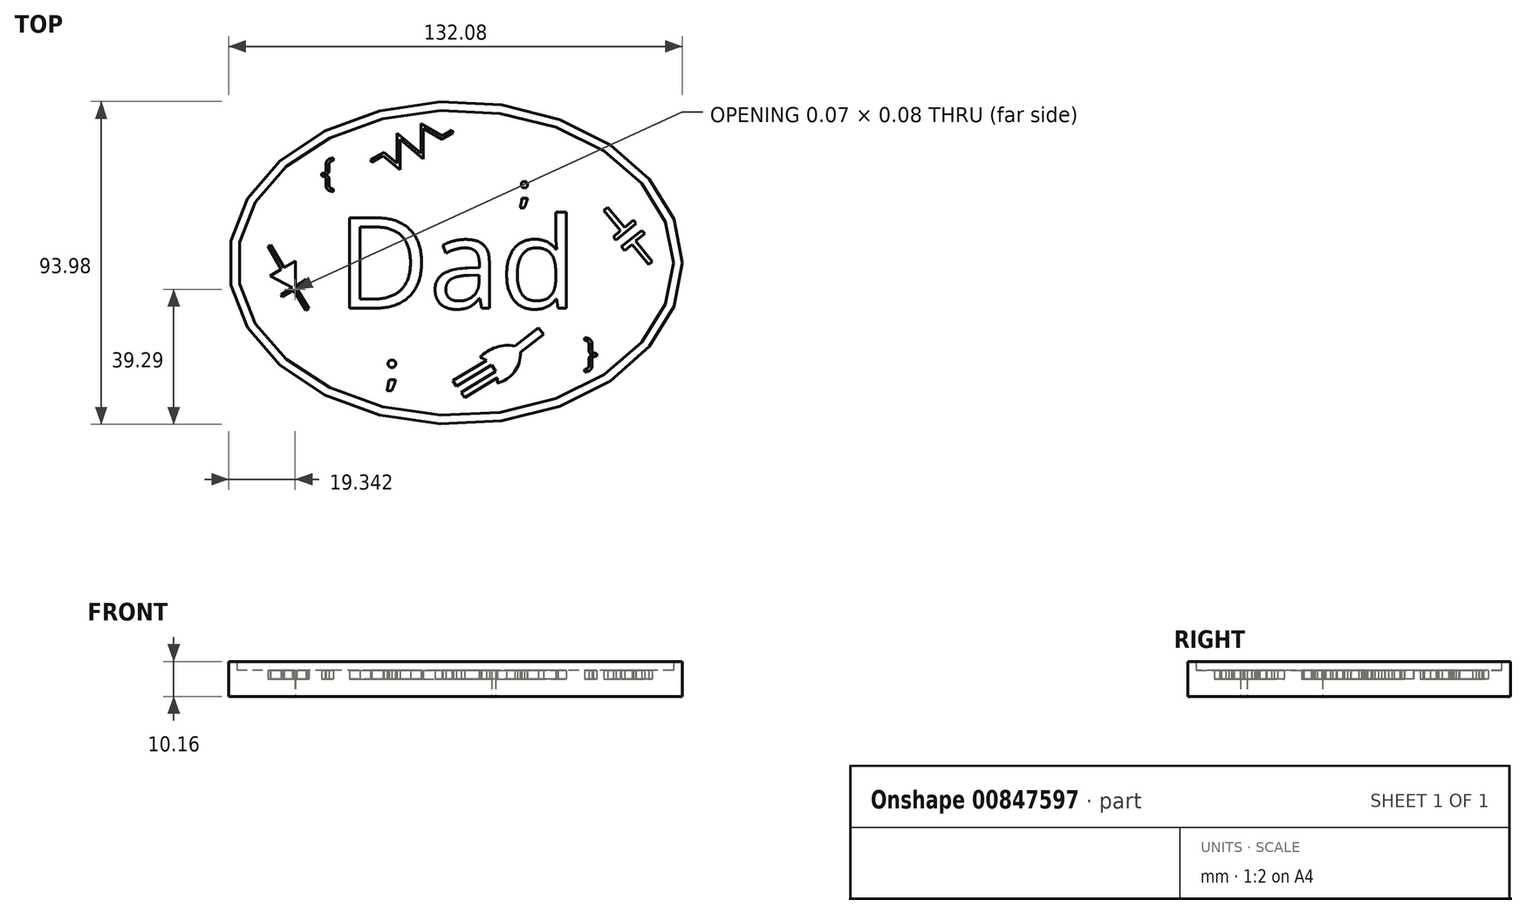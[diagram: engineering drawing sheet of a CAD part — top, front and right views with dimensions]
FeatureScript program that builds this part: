
annotation { "Feature Type Name" : "Feature", "Feature Type Description" : "" }
export const myFeature = defineFeature(function(context is Context, id is Id, definition is map)
    precondition{}
    {
        {
            var Q0;
            Q0=qCreatedBy(makeId("Top.planeOp"),FACE);
            var sketch = newSketch(context, id + "F0", { "sketchPlane" : qUnion([Q0])});
            skEllipse(sketch, "E0", {"center": v(-70.5, 33.66) * mm, "majorRadius": 63.5 * mm, "minorRadius": 44.45 * mm, "majorAxis": v(1, 0)});
            skEllipse(sketch, "E1", {"center": v(-70.5, 33.66) * mm, "majorRadius": 66.04 * mm, "minorRadius": 47 * mm, "majorAxis": v(1, 0)});
            skPoint(sketch, "E2.endSnap0", {"position": v(-134, 33.66) * mm});
            skText(sketch, "E3", { "text": "Dad", "fontName": "OpenSans-Regular.ttf"});
            skText(sketch, "E4", { "text": "{", "fontName": "OpenSans-Regular.ttf"});
            skText(sketch, "E5", { "text": "}", "fontName": "OpenSans-Regular.ttf"});
            skText(sketch, "E6", { "text": ";", "fontName": "OpenSans-Bold.ttf"});
            skText(sketch, "E7", { "text": ";", "fontName": "OpenSans-Bold.ttf"});
            skLineSegment(sketch, "E8", {"start": v(-124.5, 29.9) * mm, "end": v(-117.16, 34.26) * mm});
            skLineSegment(sketch, "E9", {"start": v(-117.16, 25.92) * mm, "end": v(-124.5, 29.9) * mm});
            skLineSegment(sketch, "E10", {"start": v(-117.16, 25.92) * mm, "end": v(-117.16, 34.26) * mm});
            skLineSegment(sketch, "E11", {"start": v(-120.84, 32.08) * mm, "end": v(-120.4, 32.33) * mm});
            skLineSegment(sketch, "E12", {"start": v(-121.27, 31.82) * mm, "end": v(-125.17, 38.37) * mm});
            skLineSegment(sketch, "E13", {"start": v(-125.17, 38.37) * mm, "end": v(-124.36, 38.85) * mm});
            skLineSegment(sketch, "E14", {"start": v(-124.36, 38.85) * mm, "end": v(-120.4, 32.33) * mm});
            skLineSegment(sketch, "E15", {"start": v(-118.04, 26.4) * mm, "end": v(-114.08, 19.88) * mm});
            skLineSegment(sketch, "E16", {"start": v(-114.08, 19.88) * mm, "end": v(-113.21, 20.4) * mm});
            skLineSegment(sketch, "E17", {"start": v(-113.21, 20.4) * mm, "end": v(-117.16, 26.9) * mm});
            skLineSegment(sketch, "E18", {"start": v(-118.04, 26.4) * mm, "end": v(-117.16, 26.9) * mm});
            skLineSegment(sketch, "E19", {"start": v(-117.16, 26.9) * mm, "end": v(-113.9, 28.87) * mm});
            skLineSegment(sketch, "E20", {"start": v(-113.9, 28.87) * mm, "end": v(-113.51, 28.22) * mm});
            skLineSegment(sketch, "E21", {"start": v(-113.51, 28.22) * mm, "end": v(-120.89, 23.73) * mm});
            skLineSegment(sketch, "E22", {"start": v(-120.89, 23.73) * mm, "end": v(-121.29, 24.38) * mm});
            skLineSegment(sketch, "E23", {"start": v(-121.29, 24.38) * mm, "end": v(-118.04, 26.4) * mm});
            skLineSegment(sketch, "E24", {"start": v(-95.24, 63.62) * mm, "end": v(-94.86, 62.96) * mm});
            skLineSegment(sketch, "E25", {"start": v(-94.86, 62.96) * mm, "end": v(-91.56, 64.86) * mm});
            skLineSegment(sketch, "E26", {"start": v(-91.56, 64.86) * mm, "end": v(-86.7, 60.78) * mm});
            skLineSegment(sketch, "E27", {"start": v(-86.7, 60.78) * mm, "end": v(-86.7, 69.67) * mm});
            skLineSegment(sketch, "E28", {"start": v(-86.7, 69.67) * mm, "end": v(-79.88, 63.96) * mm});
            skLineSegment(sketch, "E29", {"start": v(-79.88, 63.96) * mm, "end": v(-79.88, 72.85) * mm});
            skLineSegment(sketch, "E30", {"start": v(-79.88, 72.85) * mm, "end": v(-74.38, 69.67) * mm});
            skLineSegment(sketch, "E31", {"start": v(-74.38, 69.67) * mm, "end": v(-71.08, 71.57) * mm});
            skLineSegment(sketch, "E32", {"start": v(-95.24, 63.62) * mm, "end": v(-91.34, 65.87) * mm});
            skLineSegment(sketch, "E33", {"start": v(-91.34, 65.87) * mm, "end": v(-87.55, 62.7) * mm});
            skLineSegment(sketch, "E34", {"start": v(-87.55, 62.7) * mm, "end": v(-87.55, 71.4) * mm});
            skLineSegment(sketch, "E35", {"start": v(-87.55, 71.4) * mm, "end": v(-80.6, 65.56) * mm});
            skLineSegment(sketch, "E36", {"start": v(-80.6, 65.56) * mm, "end": v(-80.6, 74.19) * mm});
            skLineSegment(sketch, "E37", {"start": v(-80.6, 74.19) * mm, "end": v(-74.36, 70.59) * mm});
            skLineSegment(sketch, "E38", {"start": v(-74.36, 70.59) * mm, "end": v(-71.48, 72.25) * mm});
            skLineSegment(sketch, "E39", {"start": v(-71.48, 72.25) * mm, "end": v(-71.08, 71.57) * mm});
            skLineSegment(sketch, "E40", {"start": v(-24.58, 41.24) * mm, "end": v(-18.74, 46.14) * mm});
            skLineSegment(sketch, "E41", {"start": v(-18.74, 46.14) * mm, "end": v(-17.92, 45.17) * mm});
            skLineSegment(sketch, "E42", {"start": v(-17.92, 45.17) * mm, "end": v(-23.76, 40.27) * mm});
            skLineSegment(sketch, "E43", {"start": v(-23.76, 40.27) * mm, "end": v(-24.58, 41.24) * mm});
            skLineSegment(sketch, "E44", {"start": v(-22.2, 38.38) * mm, "end": v(-16.25, 43.14) * mm});
            skLineSegment(sketch, "E45", {"start": v(-16.25, 43.14) * mm, "end": v(-15.43, 42.17) * mm});
            skLineSegment(sketch, "E46", {"start": v(-15.43, 42.17) * mm, "end": v(-21.27, 37.27) * mm});
            skLineSegment(sketch, "E47", {"start": v(-21.27, 37.27) * mm, "end": v(-22.2, 38.38) * mm});
            skLineSegment(sketch, "E48", {"start": v(-22.44, 43.04) * mm, "end": v(-27.33, 48.88) * mm});
            skLineSegment(sketch, "E49", {"start": v(-27.33, 48.88) * mm, "end": v(-26.15, 49.87) * mm});
            skLineSegment(sketch, "E50", {"start": v(-26.15, 49.87) * mm, "end": v(-21.26, 44.03) * mm});
            skLineSegment(sketch, "E51", {"start": v(-19.1, 39.09) * mm, "end": v(-14.21, 33.25) * mm});
            skLineSegment(sketch, "E52", {"start": v(-14.21, 33.25) * mm, "end": v(-13.24, 34.06) * mm});
            skLineSegment(sketch, "E53", {"start": v(-13.24, 34.06) * mm, "end": v(-18, 40.01) * mm});
            skArc(sketch, "E54", {"start": v(-58.37, -1.38) * mm, "mid": v(-59.5, 3.29) * mm, "end": v(-63.34, 6.15) * mm});
            skArc(sketch, "E55", {"start": v(-51.76, 9.1) * mm, "mid": v(-57.98, 9.31) * mm, "end": v(-63.34, 6.15) * mm});
            skArc(sketch, "E56", {"start": v(-58.37, -1.38) * mm, "mid": v(-52.97, 2.53) * mm, "end": v(-51.76, 9.1) * mm});
            skLineSegment(sketch, "E57", {"start": v(-53.22, 9.47) * mm, "end": v(-46.35, 14.8) * mm});
            skLineSegment(sketch, "E58", {"start": v(-46.35, 14.8) * mm, "end": v(-44.87, 12.88) * mm});
            skLineSegment(sketch, "E59", {"start": v(-44.87, 12.88) * mm, "end": v(-51.59, 7.67) * mm});
            skLineSegment(sketch, "E60", {"start": v(-71.23, -0.6) * mm, "end": v(-61.51, 5.3) * mm});
            skLineSegment(sketch, "E61", {"start": v(-71.23, -0.6) * mm, "end": v(-70.23, -2.24) * mm});
            skLineSegment(sketch, "E62", {"start": v(-70.23, -2.24) * mm, "end": v(-60, 3.96) * mm});
            skLineSegment(sketch, "E63", {"start": v(-60, 3.96) * mm, "end": v(-58.85, 2.07) * mm});
            skLineSegment(sketch, "E64", {"start": v(-58.85, 2.07) * mm, "end": v(-68.81, -3.97) * mm});
            skLineSegment(sketch, "E65", {"start": v(-68.81, -3.97) * mm, "end": v(-67.86, -5.53) * mm});
            skLineSegment(sketch, "E66", {"start": v(-67.86, -5.53) * mm, "end": v(-58.38, 0.22) * mm});
            const initialGuessF0  = {"E3": [-0.10497, 0.02048, 1, 0, 0.0265], "E4": [-0.10988, 0.0562, 1, 0, 0.00803], "E5": [-0.03333, 0.00376, 1, 0, 0.0082], "E6": [-0.05202, 0.05118, 1, 0, 0.00798], "E7": [-0.09087, -0.00184, 1, 0, 0.00935]};
            skSetInitialGuess(sketch, initialGuessF0);
            skSolve(sketch);
        }
        {
            var Q0;
            Q0=makeQuery(id+"F0.imprint","IMPRINT",FACE,{"disambiguationData":[TD([[makeQuery(id+"F0.imprint","IMPRINT",EDGE,{"derivedFrom":sQuery(id+"F0.wireOp",EDGE,"E0")}),-1.0]])]});
            extrude(context, id + "F1", {"entities" : qUnion([Q0]), "depth" : 10.16 * mm, "offsetDistance" : 25.4 * mm});
        }
        {
            var Q0;
            Q0=makeQuery(id+"F0.imprint","IMPRINT",FACE,{"disambiguationData":[TD([[makeQuery(id+"F0.imprint","IMPRINT",EDGE,{"derivedFrom":sQuery(id+"F0.wireOp",EDGE,"E0")}),1.0]])]});
            extrude(context, id + "F2", {"entities" : qUnion([Q0]), "operationType" : NewBodyOperationType.ADD, "depth" : 7.62 * mm, "offsetDistance" : 25.4 * mm});
        }
        {
            var Q0;
            Q0=makeQuery(id+"F0.imprint","IMPRINT",FACE,{"disambiguationData":[TD([[makeQuery(id+"F0.imprint","IMPRINT",EDGE,{"derivedFrom":sQuery(id+"F0.wireOp",EDGE,"E4.sketch_text.stroke-0")}),-1.0]])]});
            extrude(context, id + "F3", {"entities" : qUnion([Q0]), "operationType" : NewBodyOperationType.ADD, "depth" : 5.08 * mm, "offsetDistance" : 25.4 * mm});
        }
        {
            var Q0;
            {var subQ0=sQuery(id+"F0.wireOp",EDGE,"E55");var subQ1=sQuery(id+"F0.wireOp",EDGE,"E54");var subQ2=makeQuery(id+"F0.imprint","INTERSECT",VERTEX,{"derivedFrom":[subQ1,subQ0]});Q0=makeQuery(id+"F0.imprint","IMPRINT",FACE,{"disambiguationData":[TD([[makeQuery(id+"F0.imprint","IMPRINT",EDGE,{"disambiguationData":[TD([[subQ2,1.0]])],"derivedFrom":subQ1}),-1.0]])]});}
            var Q1;
            {var subQ0=sQuery(id+"F0.wireOp",EDGE,"E57");Q1=makeQuery(id+"F0.imprint","IMPRINT",FACE,{"disambiguationData":[TD([[makeQuery(id+"F0.imprint","IMPRINT",EDGE,{"derivedFrom":subQ0}),-1.0]])]});}
            var Q2;
            {var subQ0=sQuery(id+"F0.wireOp",EDGE,"E60");Q2=makeQuery(id+"F0.imprint","IMPRINT",FACE,{"disambiguationData":[TD([[makeQuery(id+"F0.imprint","IMPRINT",EDGE,{"derivedFrom":subQ0}),-1.0]])]});}
            var Q3;
            {var subQ2=sQuery(id+"F0.wireOp",EDGE,"E64");Q3=makeQuery(id+"F0.imprint","IMPRINT",FACE,{"disambiguationData":[TD([[makeQuery(id+"F0.imprint","IMPRINT",EDGE,{"derivedFrom":subQ2}),1.0]])]});}
            extrude(context, id + "F4", {"entities" : qUnion([Q0, Q1, Q2, Q3]), "operationType" : NewBodyOperationType.ADD, "depth" : 5.08 * mm, "offsetDistance" : 25.4 * mm});
        }
        {
            var Q0;
            Q0=makeQuery(id+"F0.imprint","IMPRINT",FACE,{"disambiguationData":[TD([[makeQuery(id+"F0.imprint","IMPRINT",EDGE,{"derivedFrom":sQuery(id+"F0.wireOp",EDGE,"E7.sketch_text.stroke-5")}),-1.0]])]});
            var Q1;
            Q1=makeQuery(id+"F0.imprint","IMPRINT",FACE,{"disambiguationData":[TD([[makeQuery(id+"F0.imprint","IMPRINT",EDGE,{"derivedFrom":sQuery(id+"F0.wireOp",EDGE,"E7.sketch_text.stroke-0")}),-1.0]])]});
            extrude(context, id + "F5", {"entities" : qUnion([Q0, Q1]), "operationType" : NewBodyOperationType.ADD, "depth" : 5.08 * mm, "offsetDistance" : 25.4 * mm});
        }
        {
            var Q0;
            {var subQ0=sQuery(id+"F0.wireOp",EDGE,"E12");Q0=makeQuery(id+"F0.imprint","IMPRINT",FACE,{"disambiguationData":[TD([[makeQuery(id+"F0.imprint","IMPRINT",EDGE,{"derivedFrom":subQ0}),-1.0]])]});}
            var Q1;
            {var subQ8=sQuery(id+"F0.wireOp",EDGE,"E18");Q1=makeQuery(id+"F0.imprint","IMPRINT",FACE,{"disambiguationData":[TD([[makeQuery(id+"F0.imprint","IMPRINT",EDGE,{"derivedFrom":subQ8}),1.0]])]});}
            var Q2;
            {var subQ0=sQuery(id+"F0.wireOp",EDGE,"E19");Q2=makeQuery(id+"F0.imprint","IMPRINT",FACE,{"disambiguationData":[TD([[makeQuery(id+"F0.imprint","IMPRINT",EDGE,{"derivedFrom":subQ0}),-1.0]])]});}
            var Q3;
            {var subQ0=sQuery(id+"F0.wireOp",EDGE,"E18");Q3=makeQuery(id+"F0.imprint","IMPRINT",FACE,{"disambiguationData":[TD([[makeQuery(id+"F0.imprint","IMPRINT",EDGE,{"derivedFrom":subQ0}),-1.0]])]});}
            var Q4;
            {var subQ4=sQuery(id+"F0.wireOp",EDGE,"E22");Q4=makeQuery(id+"F0.imprint","IMPRINT",FACE,{"disambiguationData":[TD([[makeQuery(id+"F0.imprint","IMPRINT",EDGE,{"derivedFrom":subQ4}),-1.0]])]});}
            var Q5;
            {var subQ0=sQuery(id+"F0.wireOp",EDGE,"E16");Q5=makeQuery(id+"F0.imprint","IMPRINT",FACE,{"disambiguationData":[TD([[makeQuery(id+"F0.imprint","IMPRINT",EDGE,{"derivedFrom":subQ0}),1.0]])]});}
            var Q6;
            {var subQ1=sQuery(id+"F0.wireOp",EDGE,"E9");var subQ3=sQuery(id+"F0.wireOp",EDGE,"E21");var subQ4=makeQuery(id+"F0.imprint","INTERSECT",VERTEX,{"derivedFrom":[subQ1,subQ3]});Q6=makeQuery(id+"F0.imprint","IMPRINT",FACE,{"disambiguationData":[TD([[makeQuery(id+"F0.imprint","IMPRINT",EDGE,{"disambiguationData":[TD([[subQ4,-1.0]])],"derivedFrom":subQ3}),-1.0]])]});}
            var Q7;
            {var subQ1=sQuery(id+"F0.wireOp",EDGE,"E10");var subQ3=sQuery(id+"F0.wireOp",EDGE,"E21");var subQ4=makeQuery(id+"F0.imprint","INTERSECT",VERTEX,{"derivedFrom":[subQ1,subQ3]});Q7=makeQuery(id+"F0.imprint","IMPRINT",FACE,{"disambiguationData":[TD([[makeQuery(id+"F0.imprint","IMPRINT",EDGE,{"disambiguationData":[TD([[subQ4,1.0]])],"derivedFrom":subQ3}),-1.0]])]});}
            extrude(context, id + "F6", {"entities" : qUnion([Q0, Q1, Q2, Q3, Q4, Q5, Q6, Q7]), "operationType" : NewBodyOperationType.ADD, "depth" : 5.08 * mm, "offsetDistance" : 25.4 * mm});
        }
        {
            var Q0;
            Q0=makeQuery(id+"F0.imprint","IMPRINT",FACE,{"disambiguationData":[TD([[makeQuery(id+"F0.imprint","IMPRINT",EDGE,{"derivedFrom":sQuery(id+"F0.wireOp",EDGE,"E24")}),1.0]])]});
            var Q1;
            Q1=makeQuery(id+"F0.imprint","IMPRINT",FACE,{"disambiguationData":[TD([[makeQuery(id+"F0.imprint","IMPRINT",EDGE,{"derivedFrom":sQuery(id+"F0.wireOp",EDGE,"E6.sketch_text.stroke-5")}),-1.0]])]});
            var Q2;
            Q2=makeQuery(id+"F0.imprint","IMPRINT",FACE,{"disambiguationData":[TD([[makeQuery(id+"F0.imprint","IMPRINT",EDGE,{"derivedFrom":sQuery(id+"F0.wireOp",EDGE,"E6.sketch_text.stroke-0")}),-1.0]])]});
            extrude(context, id + "F7", {"entities" : qUnion([Q0, Q1, Q2]), "operationType" : NewBodyOperationType.ADD, "depth" : 5.08 * mm, "offsetDistance" : 25.4 * mm});
        }
        {
            var Q0;
            {var subQ2=sQuery(id+"F0.wireOp",EDGE,"E48");Q0=makeQuery(id+"F0.imprint","IMPRINT",FACE,{"disambiguationData":[TD([[makeQuery(id+"F0.imprint","IMPRINT",EDGE,{"derivedFrom":subQ2}),-1.0]])]});}
            var Q1;
            {var subQ0=sQuery(id+"F0.wireOp",EDGE,"E41");Q1=makeQuery(id+"F0.imprint","IMPRINT",FACE,{"disambiguationData":[TD([[makeQuery(id+"F0.imprint","IMPRINT",EDGE,{"derivedFrom":subQ0}),-1.0]])]});}
            var Q2;
            Q2=makeQuery(id+"F0.imprint","IMPRINT",FACE,{"disambiguationData":[TD([[makeQuery(id+"F0.imprint","IMPRINT",EDGE,{"derivedFrom":sQuery(id+"F0.wireOp",EDGE,"E44")}),-1.0]])]});
            var Q3;
            {var subQ0=sQuery(id+"F0.wireOp",EDGE,"E51");Q3=makeQuery(id+"F0.imprint","IMPRINT",FACE,{"disambiguationData":[TD([[makeQuery(id+"F0.imprint","IMPRINT",EDGE,{"derivedFrom":subQ0}),1.0]])]});}
            var Q4;
            Q4=makeQuery(id+"F0.imprint","IMPRINT",FACE,{"disambiguationData":[TD([[makeQuery(id+"F0.imprint","IMPRINT",EDGE,{"derivedFrom":sQuery(id+"F0.wireOp",EDGE,"E5.sketch_text.stroke-0")}),-1.0]])]});
            extrude(context, id + "F8", {"entities" : qUnion([Q0, Q1, Q2, Q3, Q4]), "operationType" : NewBodyOperationType.ADD, "depth" : 5.08 * mm, "offsetDistance" : 25.4 * mm});
        }
        {
            var Q0;
            Q0=makeQuery(id+"F0.imprint","IMPRINT",FACE,{"disambiguationData":[TD([[makeQuery(id+"F0.imprint","IMPRINT",EDGE,{"derivedFrom":sQuery(id+"F0.wireOp",EDGE,"E3.sketch_text.stroke-0")}),-1.0]])]});
            var Q1;
            Q1=makeQuery(id+"F0.imprint","IMPRINT",FACE,{"disambiguationData":[TD([[makeQuery(id+"F0.imprint","IMPRINT",EDGE,{"derivedFrom":sQuery(id+"F0.wireOp",EDGE,"E3.sketch_text.stroke-14")}),-1.0]])]});
            var Q2;
            Q2=makeQuery(id+"F0.imprint","IMPRINT",FACE,{"disambiguationData":[TD([[makeQuery(id+"F0.imprint","IMPRINT",EDGE,{"derivedFrom":sQuery(id+"F0.wireOp",EDGE,"E3.sketch_text.stroke-41")}),-1.0]])]});
            extrude(context, id + "F9", {"entities" : qUnion([Q0, Q1, Q2]), "operationType" : NewBodyOperationType.ADD, "depth" : 5.08 * mm, "offsetDistance" : 25.4 * mm});
        }
        {
            var Q0;
            Q0=makeQuery(id+"F0.imprint","IMPRINT",FACE,{"disambiguationData":[TD([[makeQuery(id+"F0.imprint","IMPRINT",EDGE,{"derivedFrom":sQuery(id+"F0.wireOp",EDGE,"E3.sketch_text.stroke-7")}),1.0]])]});
            var Q1;
            Q1=makeQuery(id+"F0.imprint","IMPRINT",FACE,{"disambiguationData":[TD([[makeQuery(id+"F0.imprint","IMPRINT",EDGE,{"derivedFrom":sQuery(id+"F0.wireOp",EDGE,"E3.sketch_text.stroke-33")}),1.0]])]});
            var Q2;
            Q2=makeQuery(id+"F0.imprint","IMPRINT",FACE,{"disambiguationData":[TD([[makeQuery(id+"F0.imprint","IMPRINT",EDGE,{"derivedFrom":sQuery(id+"F0.wireOp",EDGE,"E3.sketch_text.stroke-56")}),1.0]])]});
            extrude(context, id + "F10", {"entities" : qUnion([Q0, Q1, Q2]), "operationType" : NewBodyOperationType.ADD, "depth" : 7.62 * mm, "offsetDistance" : 25.4 * mm});
        }
    });
